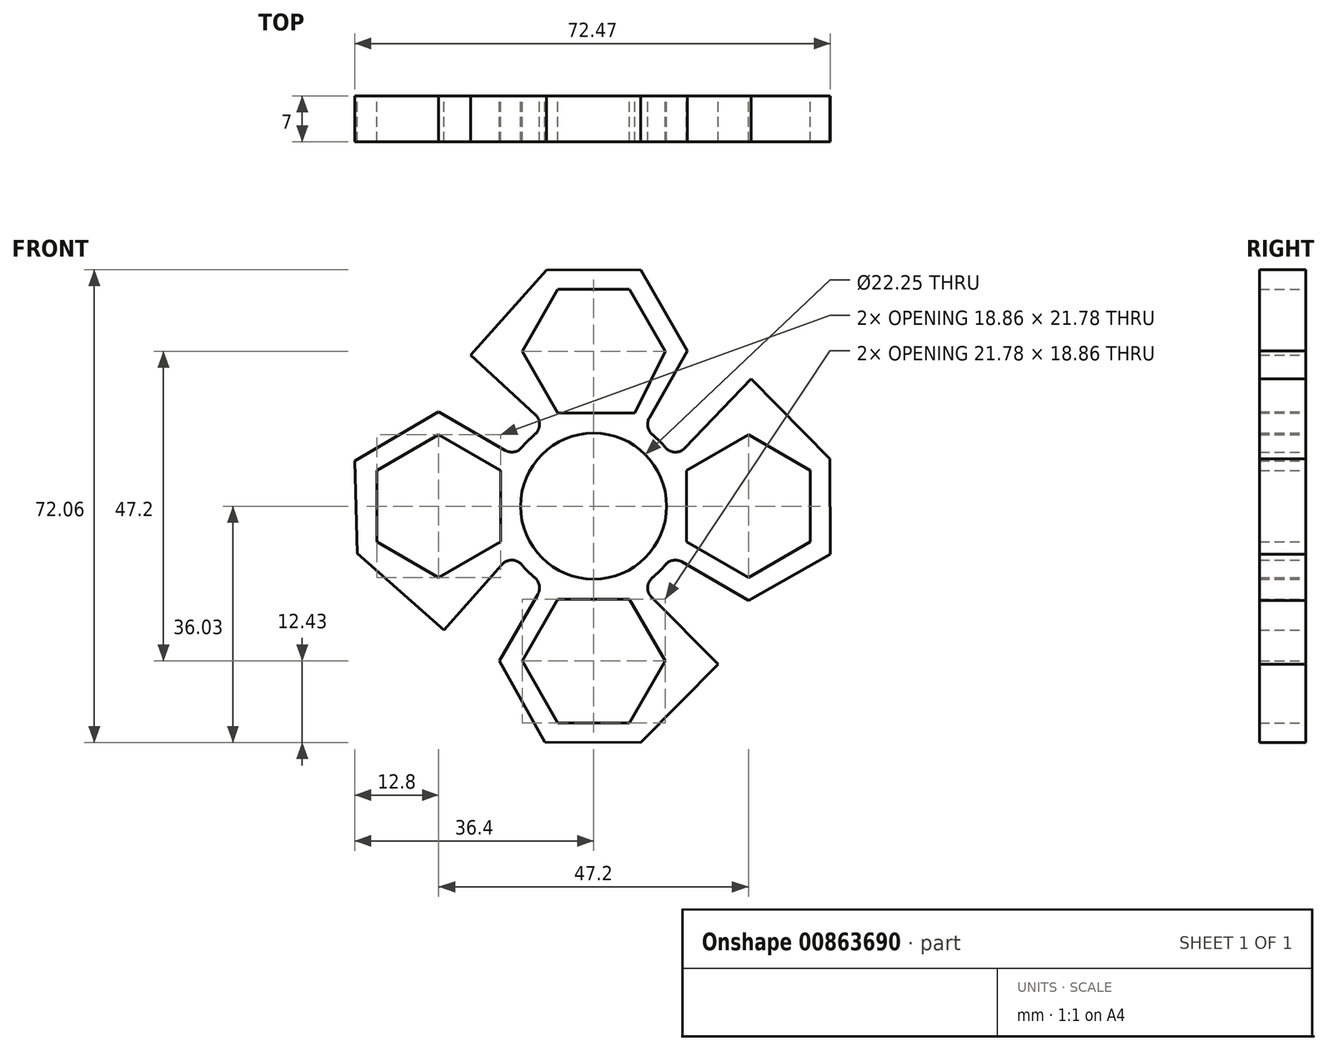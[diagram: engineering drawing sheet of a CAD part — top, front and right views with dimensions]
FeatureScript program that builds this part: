
annotation { "Feature Type Name" : "Feature", "Feature Type Description" : "" }
export const myFeature = defineFeature(function(context is Context, id is Id, definition is map)
    precondition{}
    {
        {
            var Q0;
            Q0=qCreatedBy(makeId("Front.planeOp"),FACE);
            var sketch = newSketch(context, id + "F0", { "sketchPlane" : qUnion([Q0])});
            skCircle(sketch, "E0", {"center": v(0, 0) * mm, "radius": 11.12 * mm});
            skLineSegment(sketch, "E1.0", {"start": v(-5.44, 33.03) * mm, "end": v(5.44, 33.03) * mm});
            skLineSegment(sketch, "E1.1", {"start": v(5.44, 33.03) * mm, "end": v(10.89, 23.6) * mm});
            skLineSegment(sketch, "E1.2", {"start": v(10.89, 23.6) * mm, "end": v(6.3, 14.2) * mm});
            skLineSegment(sketch, "E1.3", {"start": v(6.3, 14.2) * mm, "end": v(-5.44, 14.17) * mm});
            skLineSegment(sketch, "E1.4", {"start": v(-5.44, 14.17) * mm, "end": v(-10.89, 23.6) * mm});
            skLineSegment(sketch, "E1.5", {"start": v(-10.89, 23.6) * mm, "end": v(-5.44, 33.03) * mm});
            skPoint(sketch, "E1.0.midPoint", {"position": v(0, 33.03) * mm});
            skLineSegment(sketch, "E2.0", {"start": v(-7.18, 36) * mm, "end": v(7.18, 36.03) * mm});
            skLineSegment(sketch, "E2.1", {"start": v(7.18, 36.03) * mm, "end": v(14.25, 23.66) * mm});
            skLineSegment(sketch, "E2.2", {"start": v(14.25, 23.66) * mm, "end": v(8.5, 13.45) * mm});
            skLineSegment(sketch, "E2.4", {"start": v(-8.87, 13.93) * mm, "end": v(-18.7, 23.05) * mm});
            skLineSegment(sketch, "E2.5", {"start": v(-18.7, 23.05) * mm, "end": v(-7.18, 36) * mm});
            skPoint(sketch, "E2.0.midPoint", {"position": v(0, 36.02) * mm});
            skLineSegment(sketch, "E3.1.0", {"start": v(-33.03, 5.44) * mm, "end": v(-23.6, 10.89) * mm});
            skPoint(sketch, "E3.1.1", {"position": v(-33.03, 0) * mm});
            skLineSegment(sketch, "E3.1.2", {"start": v(-23.6, -10.89) * mm, "end": v(-33.03, -5.44) * mm});
            skLineSegment(sketch, "E3.1.3", {"start": v(-22.82, -18.91) * mm, "end": v(-36.03, -7.18) * mm});
            skPoint(sketch, "E3.1.4", {"position": v(-36.03, 0) * mm});
            skLineSegment(sketch, "E3.1.5", {"start": v(-23.6, 10.89) * mm, "end": v(-14.17, 5.44) * mm});
            skLineSegment(sketch, "E3.1.6", {"start": v(-33.03, -5.44) * mm, "end": v(-33.03, 5.44) * mm});
            skLineSegment(sketch, "E3.1.7", {"start": v(-13.96, -8.9) * mm, "end": v(-22.82, -18.91) * mm});
            skLineSegment(sketch, "E3.1.8", {"start": v(-14.17, -5.44) * mm, "end": v(-23.6, -10.89) * mm});
            skLineSegment(sketch, "E3.1.9", {"start": v(-14.17, 5.44) * mm, "end": v(-14.17, -5.44) * mm});
            skLineSegment(sketch, "E3.1.10", {"start": v(-36.4, 6.87) * mm, "end": v(-23.6, 14.35) * mm});
            skLineSegment(sketch, "E3.1.11", {"start": v(-36.03, -7.18) * mm, "end": v(-36.4, 6.87) * mm});
            skLineSegment(sketch, "E3.1.12", {"start": v(-23.6, 14.35) * mm, "end": v(-13.46, 8.5) * mm});
            skLineSegment(sketch, "E3.2.0", {"start": v(-5.44, -33.03) * mm, "end": v(-10.89, -23.6) * mm});
            skPoint(sketch, "E3.2.1", {"position": v(0, -33.03) * mm});
            skLineSegment(sketch, "E3.2.2", {"start": v(10.89, -23.6) * mm, "end": v(5.44, -33.03) * mm});
            skLineSegment(sketch, "E3.2.3", {"start": v(18.98, -24.1) * mm, "end": v(7.18, -36.03) * mm});
            skPoint(sketch, "E3.2.4", {"position": v(0, -36.03) * mm});
            skLineSegment(sketch, "E3.2.5", {"start": v(-10.89, -23.6) * mm, "end": v(-5.44, -14.17) * mm});
            skLineSegment(sketch, "E3.2.6", {"start": v(5.44, -33.03) * mm, "end": v(-5.44, -33.03) * mm});
            skLineSegment(sketch, "E3.2.7", {"start": v(8.81, -13.87) * mm, "end": v(18.98, -24.1) * mm});
            skLineSegment(sketch, "E3.2.8", {"start": v(5.44, -14.17) * mm, "end": v(10.89, -23.6) * mm});
            skLineSegment(sketch, "E3.2.9", {"start": v(-5.44, -14.17) * mm, "end": v(5.44, -14.17) * mm});
            skLineSegment(sketch, "E3.2.10", {"start": v(-7.41, -36) * mm, "end": v(-14.35, -23.6) * mm});
            skLineSegment(sketch, "E3.2.11", {"start": v(7.18, -36.03) * mm, "end": v(-7.41, -36) * mm});
            skLineSegment(sketch, "E3.2.12", {"start": v(-14.35, -23.6) * mm, "end": v(-8.5, -13.46) * mm});
            skLineSegment(sketch, "E3.3.0", {"start": v(33.03, -5.44) * mm, "end": v(23.6, -10.89) * mm});
            skPoint(sketch, "E3.3.1", {"position": v(33.03, 0) * mm});
            skLineSegment(sketch, "E3.3.2", {"start": v(23.6, 10.89) * mm, "end": v(33.03, 5.44) * mm});
            skLineSegment(sketch, "E3.3.3", {"start": v(24.02, 19.39) * mm, "end": v(36.03, 7.18) * mm});
            skPoint(sketch, "E3.3.4", {"position": v(36.03, 0) * mm});
            skLineSegment(sketch, "E3.3.5", {"start": v(23.6, -10.89) * mm, "end": v(14.17, -5.44) * mm});
            skLineSegment(sketch, "E3.3.6", {"start": v(33.03, 5.44) * mm, "end": v(33.03, -5.44) * mm});
            skLineSegment(sketch, "E3.3.7", {"start": v(13.9, 8.85) * mm, "end": v(24.02, 19.39) * mm});
            skLineSegment(sketch, "E3.3.8", {"start": v(14.17, 5.44) * mm, "end": v(23.6, 10.89) * mm});
            skLineSegment(sketch, "E3.3.9", {"start": v(14.17, -5.44) * mm, "end": v(14.17, 5.44) * mm});
            skLineSegment(sketch, "E3.3.10", {"start": v(36.07, -7.32) * mm, "end": v(23.6, -14.35) * mm});
            skLineSegment(sketch, "E3.3.11", {"start": v(36.03, 7.18) * mm, "end": v(36.07, -7.32) * mm});
            skLineSegment(sketch, "E3.3.12", {"start": v(23.6, -14.35) * mm, "end": v(13.46, -8.5) * mm});
            skArc(sketch, "E4.0", {"start": v(10.92, 8.96) * mm, "mid": v(9.99, 9.99) * mm, "end": v(8.96, 10.92) * mm});
            skArc(sketch, "E5.trimOffspring", {"start": v(8.96, -10.92) * mm, "mid": v(9.99, -9.99) * mm, "end": v(10.92, -8.96) * mm});
            skArc(sketch, "E6.trimOffspring", {"start": v(-10.92, -8.96) * mm, "mid": v(-9.99, -9.99) * mm, "end": v(-8.96, -10.92) * mm});
            skArc(sketch, "E7.trimOffspring", {"start": v(-8.96, 10.92) * mm, "mid": v(-9.99, 9.99) * mm, "end": v(-10.92, 8.96) * mm});
            skPoint(sketch, "E8.newPointB", {"position": v(-11.17, 7.18) * mm});
            skArc(sketch, "E8.filletArc", {"start": v(-13.46, 8.5) * mm, "mid": v(-12.1, 8.26) * mm, "end": v(-10.92, 8.96) * mm});
            skPoint(sketch, "E9.newPointA", {"position": v(-11.87, -6.55) * mm});
            skArc(sketch, "E9.filletArc", {"start": v(-10.92, -8.96) * mm, "mid": v(-12.43, -8.23) * mm, "end": v(-13.96, -8.9) * mm});
            skPoint(sketch, "E10.newPointB", {"position": v(-7.18, -11.17) * mm});
            skArc(sketch, "E10.filletArc", {"start": v(-8.5, -13.46) * mm, "mid": v(-8.26, -12.1) * mm, "end": v(-8.96, -10.92) * mm});
            skPoint(sketch, "E11.newPointB", {"position": v(6.66, -11.7) * mm});
            skArc(sketch, "E11.filletArc", {"start": v(8.96, -10.92) * mm, "mid": v(8.23, -12.36) * mm, "end": v(8.81, -13.87) * mm});
            skPoint(sketch, "E12.newPointB", {"position": v(11.17, -7.18) * mm});
            skArc(sketch, "E12.filletArc", {"start": v(13.46, -8.5) * mm, "mid": v(12.1, -8.26) * mm, "end": v(10.92, -8.96) * mm});
            skPoint(sketch, "E13.newPointA", {"position": v(11.76, 6.61) * mm});
            skArc(sketch, "E13.filletArc", {"start": v(10.92, 8.96) * mm, "mid": v(12.39, 8.23) * mm, "end": v(13.9, 8.85) * mm});
            skPoint(sketch, "E14.newPointB", {"position": v(7.21, 11.18) * mm});
            skArc(sketch, "E14.filletArc", {"start": v(8.5, 13.45) * mm, "mid": v(8.27, 12.1) * mm, "end": v(8.96, 10.92) * mm});
            skPoint(sketch, "E15.newPointA", {"position": v(-6.74, 11.95) * mm});
            skArc(sketch, "E15.filletArc", {"start": v(-8.96, 10.92) * mm, "mid": v(-8.23, 12.4) * mm, "end": v(-8.87, 13.93) * mm});
            skSolve(sketch);
        }
        {
            var Q0;
            Q0 = qSketchRegion(id + "F0", true);
            extrude(context, id + "F1", {"entities" : qUnion([Q0]), "depth" : 7 * mm, "offsetDistance" : 25 * mm});
        }
    });
